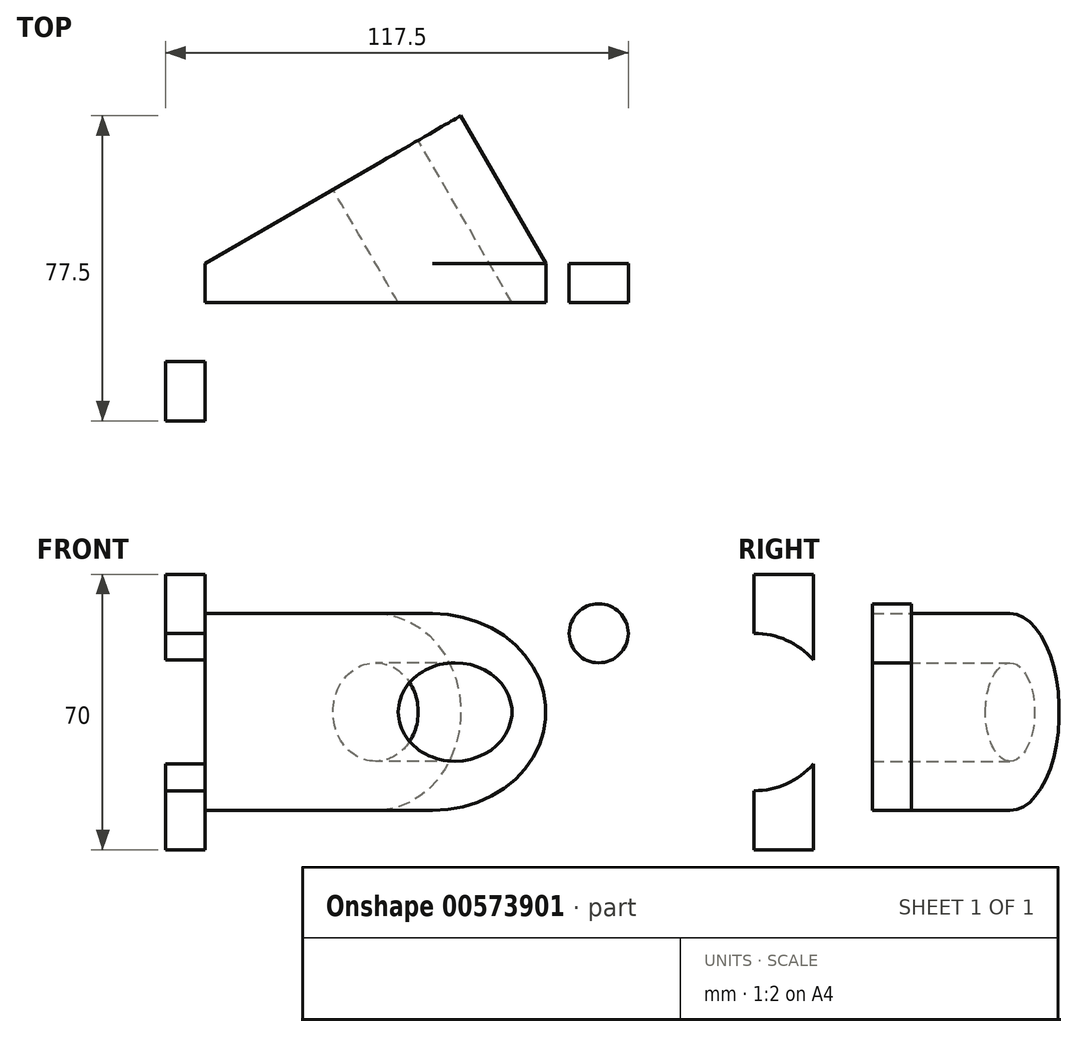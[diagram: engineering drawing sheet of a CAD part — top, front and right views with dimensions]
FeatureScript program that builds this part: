
annotation { "Feature Type Name" : "Feature", "Feature Type Description" : "" }
export const myFeature = defineFeature(function(context is Context, id is Id, definition is map)
    precondition{}
    {
        {
            var Q0;
            Q0=qCreatedBy(makeId("Top.planeOp"),FACE);
            var sketch = newSketch(context, id + "F0", { "sketchPlane" : qUnion([Q0])});
            skLineSegment(sketch, "E0", {"start": v(0, 0) * mm, "end": v(-125, 0) * mm});
            skLineSegment(sketch, "E1", {"start": v(-125, 0) * mm, "end": v(-125, -40) * mm});
            skLineSegment(sketch, "E2", {"start": v(-125, -40) * mm, "end": v(-115, -40) * mm});
            skLineSegment(sketch, "E3", {"start": v(-115, -40) * mm, "end": v(-115, -10) * mm});
            skLineSegment(sketch, "E4", {"start": v(-115, -10) * mm, "end": v(0, -10) * mm});
            skLineSegment(sketch, "E5", {"start": v(0, -10) * mm, "end": v(0, 0) * mm});
            skSolve(sketch);
        }
        {
            var Q0;
            Q0 = qSketchRegion(id + "F0", true);
            extrude(context, id + "F1", {"entities" : qUnion([Q0]), "depth" : 70 * mm, "offsetDistance" : 25 * mm});
        }
        {
            var Q0;
            Q0=makeQuery(id+"F1.opExtrude","CAP_FACE",FACE,{"disambiguationData":[OSD([sQuery(id+"F0.wireOp",EDGE,"E0"),sQuery(id+"F0.wireOp",EDGE,"E1"),sQuery(id+"F0.wireOp",EDGE,"E2"),sQuery(id+"F0.wireOp",EDGE,"E3"),sQuery(id+"F0.wireOp",EDGE,"E4"),sQuery(id+"F0.wireOp",EDGE,"E5")])],"isStart":false});
            cPlane(context, id + "F2", {"entities" : qUnion([Q0]), "cplaneType" : CPlaneType.OFFSET, "offset" : 10 * mm, "oppositeDirection" : true, "width" : 150 * mm, "height" : 150 * mm});
        }
        {
            var Q0;
            Q0=qCreatedBy(id+"F2.planeOp",FACE);
            var sketch = newSketch(context, id + "F3", { "sketchPlane" : qUnion([Q0])});
            skLineSegment(sketch, "E6", {"start": v(-28.4, 0) * mm, "end": v(-115, 0) * mm});
            skLineSegment(sketch, "E7", {"start": v(-115, 0) * mm, "end": v(-50.05, 37.5) * mm});
            skLineSegment(sketch, "E8", {"start": v(-50.05, 37.5) * mm, "end": v(-28.4, 0) * mm});
            skSolve(sketch);
        }
        {
            var Q0;
            Q0 = qSketchRegion(id + "F3", true);
            extrude(context, id + "F4", {"entities" : qUnion([Q0]), "operationType" : NewBodyOperationType.ADD, "oppositeDirection" : true, "depth" : 50 * mm, "offsetDistance" : 25 * mm});
        }
        {
            var Q0;
            Q0=makeQuery(id+"F4.opExtrude","SWEPT_FACE",FACE,{"disambiguationData":[OSD([sQuery(id+"F3.wireOp",EDGE,"E7")])]});
            var sketch = newSketch(context, id + "F5", { "sketchPlane" : qUnion([Q0])});
            skArc(sketch, "E9", {"start": v(49.6, 60) * mm, "mid": v(24.6, 35) * mm, "end": v(49.6, 10) * mm});
            skLineSegment(sketch, "E10", {"start": v(49.6, 10) * mm, "end": v(49.6, 2.65) * mm});
            skLineSegment(sketch, "E11", {"start": v(49.6, 2.65) * mm, "end": v(18.71, 2.65) * mm});
            skLineSegment(sketch, "E12", {"start": v(18.71, 2.65) * mm, "end": v(18.71, 65.16) * mm});
            skLineSegment(sketch, "E13", {"start": v(18.71, 65.16) * mm, "end": v(49.6, 65.16) * mm});
            skLineSegment(sketch, "E14", {"start": v(49.6, 65.16) * mm, "end": v(49.6, 60) * mm});
            skSolve(sketch);
        }
        {
            var Q0;
            Q0 = qSketchRegion(id + "F5", true);
            var Q1;
            Q1=makeQuery(id+"F1.opExtrude","SWEPT_FACE",FACE,{"disambiguationData":[OSD([sQuery(id+"F0.wireOp",EDGE,"E0")])]});
            extrude(context, id + "F6", {"entities" : qUnion([Q0]), "operationType" : NewBodyOperationType.REMOVE, "endBound" : BoundingType.UP_TO_SURFACE, "oppositeDirection" : true, "depth" : 25 * mm, "endBoundEntityFace" : qUnion([Q1]), "offsetDistance" : 25 * mm});
        }
        {
            var Q0;
            Q0=makeQuery(id+"F4.opExtrude","SWEPT_FACE",FACE,{"disambiguationData":[OSD([sQuery(id+"F3.wireOp",EDGE,"E7")])]});
            var sketch = newSketch(context, id + "F7", { "sketchPlane" : qUnion([Q0])});
            skCircle(sketch, "E15", {"center": v(49.6, 35) * mm, "radius": 12.5 * mm});
            skSolve(sketch);
        }
        {
            var Q0;
            Q0 = qSketchRegion(id + "F7", true);
            extrude(context, id + "F8", {"entities" : qUnion([Q0]), "operationType" : NewBodyOperationType.REMOVE, "endBound" : BoundingType.THROUGH_ALL, "oppositeDirection" : true, "depth" : 25 * mm, "offsetDistance" : 25 * mm});
        }
        {
            var Q0;
            Q0=makeQuery(id+"F1.opExtrude","CAP_EDGE",EDGE,{"disambiguationData":[OSD([sQuery(id+"F0.wireOp",EDGE,"E5")])],"isStart":false});
            var Q1;
            Q1=makeQuery(id+"F1.opExtrude","CAP_EDGE",EDGE,{"disambiguationData":[OSD([sQuery(id+"F0.wireOp",EDGE,"E5")])],"isStart":true});
            fillet(context, id + "F9", {"entities" : qUnion([Q0, Q1]), "radius" : 15 * mm, "tangentPropagation" : true, "allowEdgeOverflow" : false});
        }
        {
            var Q0;
            {var subQ0=sQuery(id+"F0.wireOp",EDGE,"E0");Q0=makeQuery(id+"F6.boolean.opBoolean","MERGE",FACE,{"derivedFrom":[makeQuery(id+"F1.opExtrude","SWEPT_FACE",FACE,{"disambiguationData":[OSD([subQ0])]}),makeQuery(id+"F6.opExtrude","CAP_FACE",FACE,{"disambiguationData":[OSD([subQ0])],"isStart":false})]});}
            var sketch = newSketch(context, id + "F10", { "sketchPlane" : qUnion([Q0])});
            skCircle(sketch, "E16", {"center": v(15, 15) * mm, "radius": 7.5 * mm});
            skCircle(sketch, "E17.MirrorC", {"center": v(15, 55) * mm, "radius": 7.5 * mm});
            skSolve(sketch);
        }
        {
            var Q0;
            Q0=makeQuery(id+"F10.imprint","IMPRINT",FACE,{"disambiguationData":[TD([[makeQuery(id+"F10.imprint","IMPRINT",EDGE,{"derivedFrom":sQuery(id+"F10.wireOp",EDGE,"E16")}),1.0]])]});
            var Q1;
            Q1=makeQuery(id+"F10.imprint","IMPRINT",FACE,{"disambiguationData":[TD([[makeQuery(id+"F10.imprint","IMPRINT",EDGE,{"derivedFrom":sQuery(id+"F10.wireOp",EDGE,"E17.MirrorC")}),-1.0]])]});
            var Q2;
            Q2=sQuery(id+"F10.wireOp",EDGE,"E16");
            var Q3;
            Q3=sQuery(id+"F10.wireOp",EDGE,"E17.MirrorC");
            extrude(context, id + "F11", {"entities" : qUnion([Q0, Q1]), "operationType" : NewBodyOperationType.REMOVE, "surfaceEntities" : qUnion([Q2, Q3]), "oppositeDirection" : true, "depth" : 25 * mm, "offsetDistance" : 25 * mm});
        }
        {
            var Q0;
            Q0=makeQuery(id+"F1.opExtrude","SWEPT_FACE",FACE,{"disambiguationData":[OSD([sQuery(id+"F0.wireOp",EDGE,"E1")])]});
            var sketch = newSketch(context, id + "F12", { "sketchPlane" : qUnion([Q0])});
            skCircle(sketch, "E18", {"center": v(40, 35) * mm, "radius": 20 * mm});
            skSolve(sketch);
        }
        {
            var Q0;
            Q0 = qSketchRegion(id + "F12", true);
            extrude(context, id + "F13", {"entities" : qUnion([Q0]), "operationType" : NewBodyOperationType.REMOVE, "oppositeDirection" : true, "depth" : 25 * mm, "offsetDistance" : 25 * mm});
        }
    });
